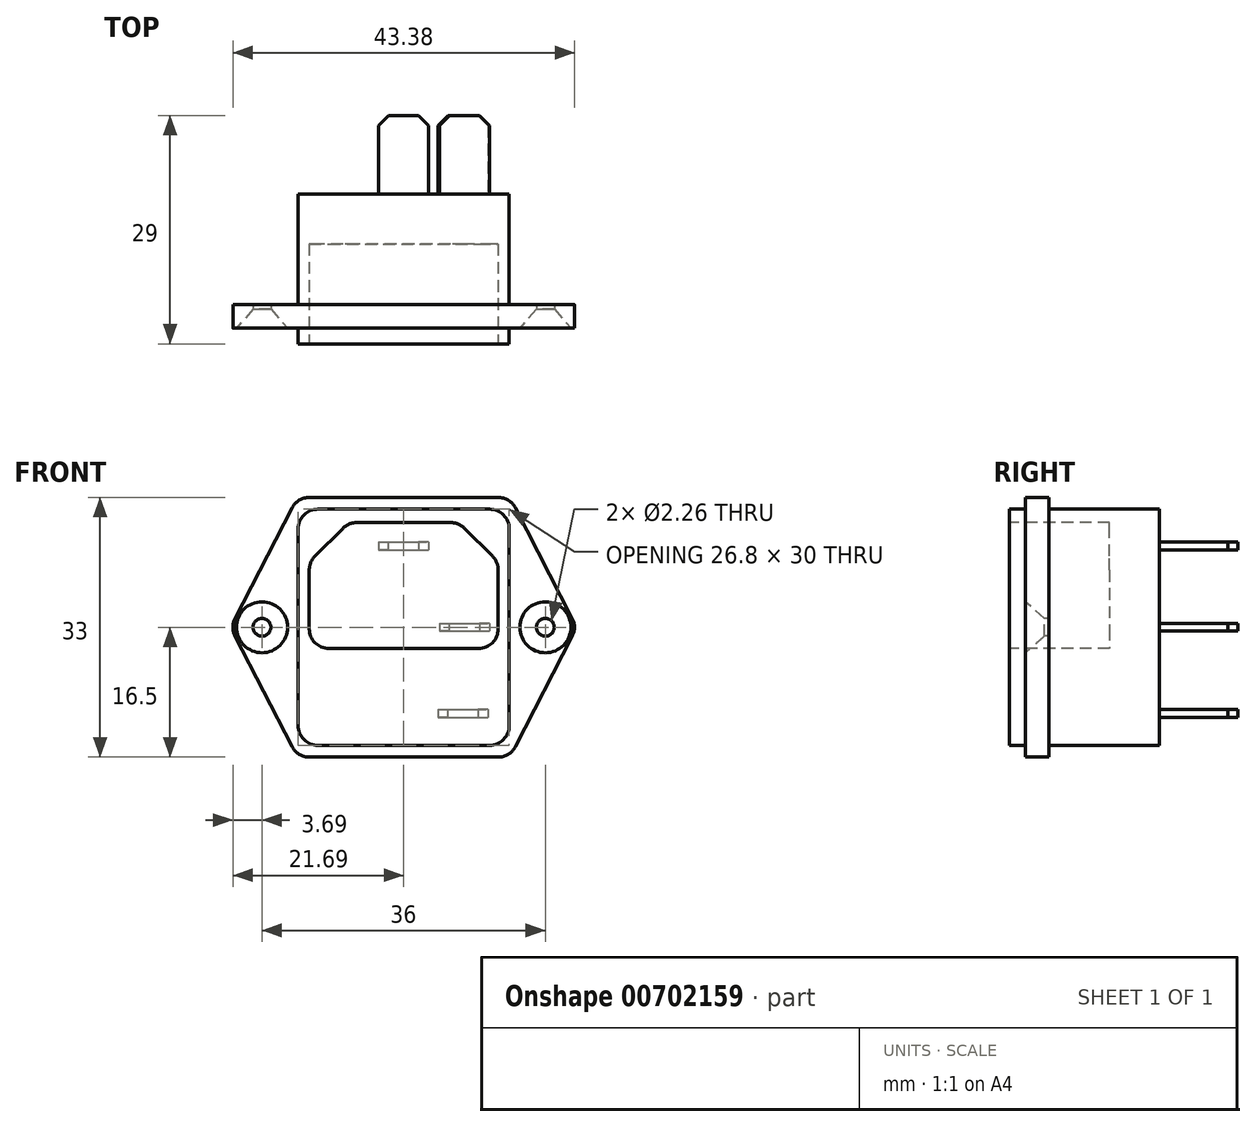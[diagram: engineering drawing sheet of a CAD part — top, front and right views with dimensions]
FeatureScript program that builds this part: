
annotation { "Feature Type Name" : "Feature", "Feature Type Description" : "" }
export const myFeature = defineFeature(function(context is Context, id is Id, definition is map)
    precondition{}
    {
        {
            var Q0;
            Q0=qCreatedBy(makeId("Front.planeOp"),FACE);
            var sketch = newSketch(context, id + "F0", { "sketchPlane" : qUnion([Q0])});
            skLineSegment(sketch, "E0", {"start": v(-13.5, 16.5) * mm, "end": v(13.5, 16.5) * mm});
            skLineSegment(sketch, "E1", {"start": v(-13.5, 16.5) * mm, "end": v(-22, 0) * mm});
            skLineSegment(sketch, "E2", {"start": v(-22, 0) * mm, "end": v(-13.5, -16.5) * mm});
            skLineSegment(sketch, "E3", {"start": v(-13.5, -16.5) * mm, "end": v(13.5, -16.5) * mm});
            skLineSegment(sketch, "E4", {"start": v(13.5, -16.5) * mm, "end": v(22, 0) * mm});
            skLineSegment(sketch, "E5", {"start": v(22, 0) * mm, "end": v(13.5, 16.5) * mm});
            skLineSegment(sketch, "E6", {"start": v(0, 16.5) * mm, "end": v(0, -16.5) * mm, "construction": true});
            skLineSegment(sketch, "E7", {"start": v(-22, 0) * mm, "end": v(0, 0) * mm, "construction": true});
            skLineSegment(sketch, "E8", {"start": v(0, 0) * mm, "end": v(22, 0) * mm, "construction": true});
            skSolve(sketch);
        }
        {
            var Q0;
            Q0 = qSketchRegion(id + "F0", true);
            extrude(context, id + "F1", {"entities" : qUnion([Q0]), "depth" : 3 * mm, "offsetDistance" : 25.4 * mm});
        }
        {
            var Q0;
            Q0=makeQuery(id+"F1.opExtrude","CAP_FACE",FACE,{"disambiguationData":[OSD([sQuery(id+"F0.wireOp",EDGE,"E0"),sQuery(id+"F0.wireOp",EDGE,"E1"),sQuery(id+"F0.wireOp",EDGE,"E2"),sQuery(id+"F0.wireOp",EDGE,"E3"),sQuery(id+"F0.wireOp",EDGE,"E4"),sQuery(id+"F0.wireOp",EDGE,"E5")])],"isStart":true});
            var sketch = newSketch(context, id + "F2", { "sketchPlane" : qUnion([Q0])});
            skLineSegment(sketch, "E9.bottom", {"start": v(-13.4, 15) * mm, "end": v(13.4, 15) * mm});
            skLineSegment(sketch, "E9.top", {"start": v(-13.4, -15) * mm, "end": v(13.4, -15) * mm});
            skLineSegment(sketch, "E9.left", {"start": v(-13.4, 15) * mm, "end": v(-13.4, -15) * mm});
            skLineSegment(sketch, "E9.right", {"start": v(13.4, 15) * mm, "end": v(13.4, -15) * mm});
            skPoint(sketch, "E9.middle", {"position": v(0, 0) * mm});
            skSolve(sketch);
        }
        {
            var Q0;
            Q0 = qSketchRegion(id + "F2", true);
            extrude(context, id + "F3", {"entities" : qUnion([Q0]), "operationType" : NewBodyOperationType.ADD, "oppositeDirection" : true, "depth" : 5 * mm, "offsetDistance" : 25.4 * mm});
        }
        {
            var Q0;
            Q0=makeQuery(id+"F1.opExtrude","CAP_FACE",FACE,{"disambiguationData":[OSD([sQuery(id+"F0.wireOp",EDGE,"E0"),sQuery(id+"F0.wireOp",EDGE,"E1"),sQuery(id+"F0.wireOp",EDGE,"E2"),sQuery(id+"F0.wireOp",EDGE,"E3"),sQuery(id+"F0.wireOp",EDGE,"E4"),sQuery(id+"F0.wireOp",EDGE,"E5")])],"isStart":true});
            var sketch = newSketch(context, id + "F4", { "sketchPlane" : qUnion([Q0])});
            skLineSegment(sketch, "E10.0.0", {"start": v(-13.4, -15) * mm, "end": v(-13.4, 15) * mm});
            skLineSegment(sketch, "E10.0.1", {"start": v(-13.4, 15) * mm, "end": v(13.4, 15) * mm});
            skLineSegment(sketch, "E10.0.2", {"start": v(13.4, 15) * mm, "end": v(13.4, -15) * mm});
            skLineSegment(sketch, "E10.0.3", {"start": v(13.4, -15) * mm, "end": v(-13.4, -15) * mm});
            skSolve(sketch);
        }
        {
            var Q0;
            Q0 = qSketchRegion(id + "F4", true);
            extrude(context, id + "F5", {"entities" : qUnion([Q0]), "operationType" : NewBodyOperationType.ADD, "depth" : 14 * mm, "offsetDistance" : 25.4 * mm});
        }
        {
            var Q0;
            Q0=makeQuery(id+"F3.opExtrude","CAP_FACE",FACE,{"disambiguationData":[OSD([sQuery(id+"F2.wireOp",EDGE,"E9.bottom"),sQuery(id+"F2.wireOp",EDGE,"E9.top"),sQuery(id+"F2.wireOp",EDGE,"E9.left"),sQuery(id+"F2.wireOp",EDGE,"E9.right")])],"isStart":false});
            var sketch = newSketch(context, id + "F6", { "sketchPlane" : qUnion([Q0])});
            skLineSegment(sketch, "E11", {"start": v(-12, -2.7) * mm, "end": v(12, -2.7) * mm});
            skLineSegment(sketch, "E12", {"start": v(12, -2.7) * mm, "end": v(12, 8.3) * mm});
            skLineSegment(sketch, "E13", {"start": v(12, 8.3) * mm, "end": v(7, 13.3) * mm});
            skLineSegment(sketch, "E14", {"start": v(7, 13.3) * mm, "end": v(-7, 13.3) * mm});
            skLineSegment(sketch, "E15", {"start": v(-7, 13.3) * mm, "end": v(-12, 8.3) * mm});
            skLineSegment(sketch, "E16", {"start": v(-12, 8.3) * mm, "end": v(-12, -2.7) * mm});
            skLineSegment(sketch, "E17", {"start": v(0, 13.3) * mm, "end": v(0, 0) * mm, "construction": true});
            skLineSegment(sketch, "E18", {"start": v(0, 0) * mm, "end": v(0, -2.7) * mm, "construction": true});
            skSolve(sketch);
        }
        {
            var Q0;
            Q0 = qSketchRegion(id + "F6", true);
            extrude(context, id + "F7", {"entities" : qUnion([Q0]), "operationType" : NewBodyOperationType.REMOVE, "oppositeDirection" : true, "depth" : 12.7 * mm, "offsetDistance" : 25.4 * mm});
        }
        {
            var Q0;
            Q0=makeQuery(id+"F5.opExtrude","CAP_FACE",FACE,{"disambiguationData":[OSD([sQuery(id+"F4.wireOp",EDGE,"E10.0.0"),sQuery(id+"F4.wireOp",EDGE,"E10.0.1"),sQuery(id+"F4.wireOp",EDGE,"E10.0.2"),sQuery(id+"F4.wireOp",EDGE,"E10.0.3")])],"isStart":false});
            var sketch = newSketch(context, id + "F8", { "sketchPlane" : qUnion([Q0])});
            skLineSegment(sketch, "E19.bottom", {"start": v(3.17, 10.81) * mm, "end": v(-3.18, 10.81) * mm});
            skLineSegment(sketch, "E19.top", {"start": v(3.18, 9.81) * mm, "end": v(-3.18, 9.81) * mm});
            skLineSegment(sketch, "E19.left", {"start": v(3.18, 10.81) * mm, "end": v(3.18, 9.81) * mm});
            skLineSegment(sketch, "E19.right", {"start": v(-3.18, 10.81) * mm, "end": v(-3.18, 9.81) * mm});
            skPoint(sketch, "E19.middle", {"position": v(0, 10.31) * mm});
            skLineSegment(sketch, "E20.bottom", {"start": v(-4.55, 0.5) * mm, "end": v(-10.9, 0.5) * mm});
            skLineSegment(sketch, "E20.top", {"start": v(-4.55, -0.5) * mm, "end": v(-10.9, -0.5) * mm});
            skLineSegment(sketch, "E20.left", {"start": v(-4.55, 0.5) * mm, "end": v(-4.55, -0.5) * mm});
            skLineSegment(sketch, "E20.right", {"start": v(-10.9, 0.5) * mm, "end": v(-10.9, -0.5) * mm});
            skPoint(sketch, "E20.middle", {"position": v(-7.73, 0) * mm});
            skLineSegment(sketch, "E21.bottom", {"start": v(-4.37, -10.44) * mm, "end": v(-10.72, -10.44) * mm});
            skLineSegment(sketch, "E21.top", {"start": v(-4.37, -11.44) * mm, "end": v(-10.72, -11.44) * mm});
            skLineSegment(sketch, "E21.left", {"start": v(-4.37, -10.44) * mm, "end": v(-4.37, -11.44) * mm});
            skLineSegment(sketch, "E21.right", {"start": v(-10.72, -10.44) * mm, "end": v(-10.72, -11.44) * mm});
            skPoint(sketch, "E21.middle", {"position": v(-7.55, -10.94) * mm});
            skSolve(sketch);
        }
        {
            var Q0;
            Q0 = qSketchRegion(id + "F8", true);
            extrude(context, id + "F9", {"entities" : qUnion([Q0]), "operationType" : NewBodyOperationType.ADD, "depth" : 10 * mm, "offsetDistance" : 25.4 * mm});
        }
        {
            var Q0;
            Q0=makeQuery(id+"F1.opExtrude","SWEPT_EDGE",EDGE,{"disambiguationData":[OSD([sQuery(id+"F0.wireOp",EDGE,"E1"),sQuery(id+"F0.wireOp",EDGE,"E2")])]});
            var Q1;
            Q1=makeQuery(id+"F1.opExtrude","SWEPT_EDGE",EDGE,{"disambiguationData":[OSD([sQuery(id+"F0.wireOp",EDGE,"E0"),sQuery(id+"F0.wireOp",EDGE,"E1")])]});
            var Q2;
            Q2=makeQuery(id+"F1.opExtrude","SWEPT_EDGE",EDGE,{"disambiguationData":[OSD([sQuery(id+"F0.wireOp",EDGE,"E0"),sQuery(id+"F0.wireOp",EDGE,"E5")])]});
            var Q3;
            Q3=makeQuery(id+"F1.opExtrude","SWEPT_EDGE",EDGE,{"disambiguationData":[OSD([sQuery(id+"F0.wireOp",EDGE,"E4"),sQuery(id+"F0.wireOp",EDGE,"E5")])]});
            var Q4;
            Q4=makeQuery(id+"F1.opExtrude","SWEPT_EDGE",EDGE,{"disambiguationData":[OSD([sQuery(id+"F0.wireOp",EDGE,"E3"),sQuery(id+"F0.wireOp",EDGE,"E4")])]});
            var Q5;
            Q5=makeQuery(id+"F1.opExtrude","SWEPT_EDGE",EDGE,{"disambiguationData":[OSD([sQuery(id+"F0.wireOp",EDGE,"E2"),sQuery(id+"F0.wireOp",EDGE,"E3")])]});
            var Q6;
            Q6=makeQuery(id+"F3.opExtrude","SWEPT_EDGE",EDGE,{"disambiguationData":[OSD([sQuery(id+"F2.wireOp",EDGE,"E9.top"),sQuery(id+"F2.wireOp",EDGE,"E9.right")])]});
            var Q7;
            Q7=makeQuery(id+"F3.opExtrude","SWEPT_EDGE",EDGE,{"disambiguationData":[OSD([sQuery(id+"F2.wireOp",EDGE,"E9.top"),sQuery(id+"F2.wireOp",EDGE,"E9.left")])]});
            var Q8;
            Q8=makeQuery(id+"F3.opExtrude","SWEPT_EDGE",EDGE,{"disambiguationData":[OSD([sQuery(id+"F2.wireOp",EDGE,"E9.bottom"),sQuery(id+"F2.wireOp",EDGE,"E9.left")])]});
            var Q9;
            Q9=makeQuery(id+"F3.opExtrude","SWEPT_EDGE",EDGE,{"disambiguationData":[OSD([sQuery(id+"F2.wireOp",EDGE,"E9.bottom"),sQuery(id+"F2.wireOp",EDGE,"E9.right")])]});
            var Q10;
            Q10=makeQuery(id+"F5.opExtrude","SWEPT_EDGE",EDGE,{"disambiguationData":[OSD([sQuery(id+"F4.wireOp",EDGE,"E10.0.1"),sQuery(id+"F4.wireOp",EDGE,"E10.0.2")])]});
            var Q11;
            Q11=makeQuery(id+"F5.opExtrude","SWEPT_EDGE",EDGE,{"disambiguationData":[OSD([sQuery(id+"F4.wireOp",EDGE,"E10.0.0"),sQuery(id+"F4.wireOp",EDGE,"E10.0.1")])]});
            var Q12;
            Q12=makeQuery(id+"F5.opExtrude","SWEPT_EDGE",EDGE,{"disambiguationData":[OSD([sQuery(id+"F4.wireOp",EDGE,"E10.0.2"),sQuery(id+"F4.wireOp",EDGE,"E10.0.3")])]});
            var Q13;
            Q13=makeQuery(id+"F5.opExtrude","SWEPT_EDGE",EDGE,{"disambiguationData":[OSD([sQuery(id+"F4.wireOp",EDGE,"E10.0.0"),sQuery(id+"F4.wireOp",EDGE,"E10.0.3")])]});
            var Q14;
            Q14=makeQuery(id+"F7.boolean.opBoolean","COPY",EDGE,{"derivedFrom":makeQuery(id+"F7.opExtrude","SWEPT_EDGE",EDGE,{"disambiguationData":[OSD([sQuery(id+"F6.wireOp",EDGE,"E15"),sQuery(id+"F6.wireOp",EDGE,"E16")])]})});
            var Q15;
            Q15=makeQuery(id+"F7.boolean.opBoolean","COPY",EDGE,{"derivedFrom":makeQuery(id+"F7.opExtrude","SWEPT_EDGE",EDGE,{"disambiguationData":[OSD([sQuery(id+"F6.wireOp",EDGE,"E14"),sQuery(id+"F6.wireOp",EDGE,"E15")])]})});
            var Q16;
            Q16=makeQuery(id+"F7.boolean.opBoolean","COPY",EDGE,{"derivedFrom":makeQuery(id+"F7.opExtrude","SWEPT_EDGE",EDGE,{"disambiguationData":[OSD([sQuery(id+"F6.wireOp",EDGE,"E13"),sQuery(id+"F6.wireOp",EDGE,"E14")])]})});
            var Q17;
            Q17=makeQuery(id+"F7.boolean.opBoolean","COPY",EDGE,{"derivedFrom":makeQuery(id+"F7.opExtrude","SWEPT_EDGE",EDGE,{"disambiguationData":[OSD([sQuery(id+"F6.wireOp",EDGE,"E12"),sQuery(id+"F6.wireOp",EDGE,"E13")])]})});
            var Q18;
            Q18=makeQuery(id+"F7.boolean.opBoolean","COPY",EDGE,{"derivedFrom":makeQuery(id+"F7.opExtrude","SWEPT_EDGE",EDGE,{"disambiguationData":[OSD([sQuery(id+"F6.wireOp",EDGE,"E11"),sQuery(id+"F6.wireOp",EDGE,"E12")])]})});
            var Q19;
            Q19=makeQuery(id+"F7.boolean.opBoolean","COPY",EDGE,{"derivedFrom":makeQuery(id+"F7.opExtrude","SWEPT_EDGE",EDGE,{"disambiguationData":[OSD([sQuery(id+"F6.wireOp",EDGE,"E11"),sQuery(id+"F6.wireOp",EDGE,"E16")])]})});
            fillet(context, id + "F10", {"entities" : qUnion([Q0, Q1, Q2, Q3, Q4, Q5, Q6, Q7, Q8, Q9, Q10, Q11, Q12, Q13, Q14, Q15, Q16, Q17, Q18, Q19]), "radius" : 2.5 * mm, "tangentPropagation" : true, "allowEdgeOverflow" : false});
        }
        {
            var Q0;
            Q0=makeQuery(id+"F9.opExtrude","CAP_EDGE",EDGE,{"disambiguationData":[OSD([sQuery(id+"F8.wireOp",EDGE,"E21.right")])],"isStart":false});
            var Q1;
            Q1=makeQuery(id+"F9.opExtrude","CAP_EDGE",EDGE,{"disambiguationData":[OSD([sQuery(id+"F8.wireOp",EDGE,"E20.right")])],"isStart":false});
            var Q2;
            Q2=makeQuery(id+"F9.opExtrude","CAP_EDGE",EDGE,{"disambiguationData":[OSD([sQuery(id+"F8.wireOp",EDGE,"E19.right")])],"isStart":false});
            var Q3;
            Q3=makeQuery(id+"F9.opExtrude","CAP_EDGE",EDGE,{"disambiguationData":[OSD([sQuery(id+"F8.wireOp",EDGE,"E19.left")])],"isStart":false});
            var Q4;
            Q4=makeQuery(id+"F9.opExtrude","CAP_EDGE",EDGE,{"disambiguationData":[OSD([sQuery(id+"F8.wireOp",EDGE,"E20.left")])],"isStart":false});
            var Q5;
            Q5=makeQuery(id+"F9.opExtrude","CAP_EDGE",EDGE,{"disambiguationData":[OSD([sQuery(id+"F8.wireOp",EDGE,"E21.left")])],"isStart":false});
            chamfer(context, id + "F11", {"entities" : qUnion([Q0, Q1, Q2, Q3, Q4, Q5]), "width" : 1.27 * mm, "tangentPropagation" : true});
        }
        {
            var Q0;
            Q0=makeQuery(id+"F1.opExtrude","CAP_FACE",FACE,{"disambiguationData":[OSD([sQuery(id+"F0.wireOp",EDGE,"E0"),sQuery(id+"F0.wireOp",EDGE,"E1"),sQuery(id+"F0.wireOp",EDGE,"E2"),sQuery(id+"F0.wireOp",EDGE,"E3"),sQuery(id+"F0.wireOp",EDGE,"E4"),sQuery(id+"F0.wireOp",EDGE,"E5")])],"isStart":false});
            var sketch = newSketch(context, id + "F12", { "sketchPlane" : qUnion([Q0])});
            skLineSegment(sketch, "E22", {"start": v(-18, 0) * mm, "end": v(0, 0) * mm});
            skLineSegment(sketch, "E23", {"start": v(0, 0) * mm, "end": v(18, 0) * mm});
            skSolve(sketch);
        }
        {
            var Q0;
            Q0=sQuery(id+"F12.wireOp",VERTEX,"E22.start");
            var Q1;
            Q1=sQuery(id+"F12.wireOp",VERTEX,"E23.end");
            var Q2;
            Q2=makeQuery(id+"F1.opExtrude","SWEPT_BODY",BODY,{"disambiguationData":[OSD([sQuery(id+"F0.wireOp",EDGE,"E0"),sQuery(id+"F0.wireOp",EDGE,"E1"),sQuery(id+"F0.wireOp",EDGE,"E2"),sQuery(id+"F0.wireOp",EDGE,"E3"),sQuery(id+"F0.wireOp",EDGE,"E4"),sQuery(id+"F0.wireOp",EDGE,"E5")])]});
            hole(context, id + "F13", {"style" : HoleStyle.C_SINK, "endStyle" : HoleEndStyle.BLIND, "standardTappedOrClearance" : lookupTablePath({ "standard" : "ANSI", "engagement" : "75%", "pitch" : "40 tpi", "size" : "#4", "type" : "Tapped" }), "standardBlindInLast" : lookupTablePath({ "standard" : "ANSI", "engagement" : "75%", "pitch" : "40 tpi", "size" : "#4", "type" : "Tapped" }), "holeDiameter" : 2.26 * mm, "cSinkDiameter" : 6.48 * mm, "cSinkAngle" : 82 * degree, "majorDiameter" : 2.84 * mm, "showTappedDepth" : true, "holeDepth" : 14.6 * mm, "isTappedThrough" : true, "tappedDepth" : 12.7 * mm, "tapClearance" : 3, "locations" : qUnion([Q0, Q1]), "scope" : qUnion([Q2])});
        }
    });
